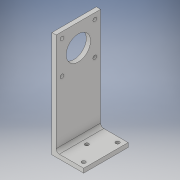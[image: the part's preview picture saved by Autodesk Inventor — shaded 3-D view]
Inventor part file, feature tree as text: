
AUTODESK INVENTOR PART (.ipt)
format: ipt  version: 2017 (Build 210142000, 142)  size: 147,968 bytes
history: native  units: in
note: dims shown in document units (in); Inventor stores cm internally (conversion verified against a paired STEP export)
features: extrude x3, sketch x3, fillet x1
ambient origin geometry x8: Origin, YZ Plane, XZ Plane, XY Plane, X Axis, Y Axis, Z Axis, Center Point
bodies: Solid1 (feature_tree)
feature tree (7):
  extrude  "Extrusion1"  Depth=1.1811in
  extrude  "Extrusion2"  Depth=1.0236in
  extrude  "Extrusion3"  Depth=3.7795in
  fillet  "Fillet1"  Radius=0.1378in
  sketch  "Sketch1"  dims[d0=3.937in d1=1.1811in]
  sketch  "Sketch2"  dims[d2=0.1575in d3=1.0236in]
  sketch  "Sketch3"  dims[d4=1.6535in d5=0.0in d6=3.7795in d7=0.1378in d8=0.2165in d9=0.2165in d10=0.1378in d11=0.2165in d12=0.2165in d14=0.1378in d15=0.1378in d16=1.2205in d17=1.2205in d18=0.2165in d19=0.2165in d20=0.9055in d21=0.8268in d22=0.6102in d23=0.1575in d24=0.0in d25=0.1378in d26=0.1378in d27=0.1378in d28=0.1969in d29=0.1969in d30=0.1969in d31=0.1969in d32=0.4724in d33=0.8268in d34=0.1575in d35=0.0in d36=0.1181in]
